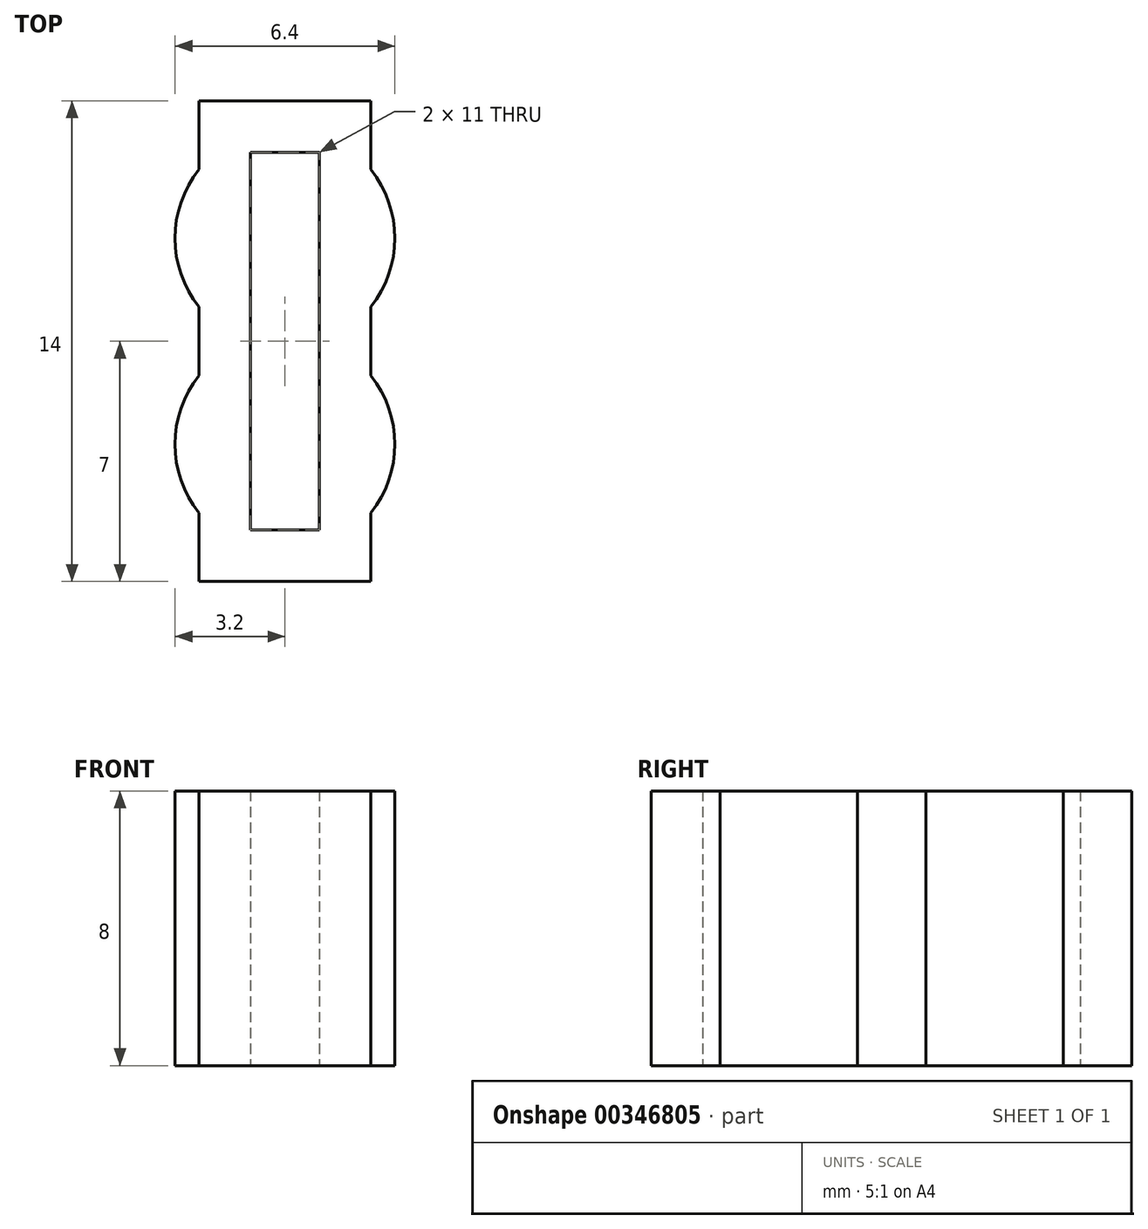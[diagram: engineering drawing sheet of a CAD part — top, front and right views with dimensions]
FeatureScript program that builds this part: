
annotation { "Feature Type Name" : "Feature", "Feature Type Description" : "" }
export const myFeature = defineFeature(function(context is Context, id is Id, definition is map)
    precondition{}
    {
        {
            var Q0;
            Q0=qCreatedBy(makeId("Top.planeOp"),FACE);
            var sketch = newSketch(context, id + "F0", { "sketchPlane" : qUnion([Q0])});
            skLineSegment(sketch, "E0.bottom", {"start": v(-2.5, 7) * mm, "end": v(2.5, 7) * mm});
            skLineSegment(sketch, "E0.top", {"start": v(-2.5, -7) * mm, "end": v(2.5, -7) * mm});
            skLineSegment(sketch, "E0.left", {"start": v(-2.5, 7) * mm, "end": v(-2.5, -7) * mm});
            skLineSegment(sketch, "E0.right", {"start": v(2.5, 7) * mm, "end": v(2.5, -7) * mm});
            skLineSegment(sketch, "E1.bottom", {"start": v(-1, 5.5) * mm, "end": v(1, 5.5) * mm});
            skLineSegment(sketch, "E1.top", {"start": v(-1, -5.5) * mm, "end": v(1, -5.5) * mm});
            skLineSegment(sketch, "E1.left", {"start": v(-1, 5.5) * mm, "end": v(-1, -5.5) * mm});
            skLineSegment(sketch, "E1.right", {"start": v(1, 5.5) * mm, "end": v(1, -5.5) * mm});
            skSolve(sketch);
        }
        {
            var Q0;
            Q0 = qSketchRegion(id + "F0", true);
            extrude(context, id + "F1", {"entities" : qUnion([Q0]), "depth" : 8 * mm});
        }
        {
            var Q0;
            Q0=qCreatedBy(makeId("Top.planeOp"),FACE);
            var sketch = newSketch(context, id + "F2", { "sketchPlane" : qUnion([Q0])});
            skArc(sketch, "E2", {"start": v(2.5, 1) * mm, "mid": v(3.2, 3) * mm, "end": v(2.5, 5) * mm});
            skArc(sketch, "E3", {"start": v(2.5, -5) * mm, "mid": v(3.2, -3) * mm, "end": v(2.5, -1) * mm});
            skLineSegment(sketch, "E4", {"start": v(2.5, 5) * mm, "end": v(2.5, 1) * mm});
            skLineSegment(sketch, "E5", {"start": v(2.5, -1) * mm, "end": v(2.5, -5) * mm});
            skArc(sketch, "E6", {"start": v(-2.5, 5) * mm, "mid": v(-3.2, 3) * mm, "end": v(-2.5, 1) * mm});
            skArc(sketch, "E7", {"start": v(-2.5, -1) * mm, "mid": v(-3.2, -3) * mm, "end": v(-2.5, -5) * mm});
            skLineSegment(sketch, "E8", {"start": v(-2.5, 5) * mm, "end": v(-2.5, 1) * mm});
            skLineSegment(sketch, "E9", {"start": v(-2.5, -1) * mm, "end": v(-2.5, -5) * mm});
            skSolve(sketch);
        }
        {
            var Q0;
            Q0 = qSketchRegion(id + "F2", true);
            extrude(context, id + "F3", {"entities" : qUnion([Q0]), "operationType" : NewBodyOperationType.ADD, "depth" : 8 * mm});
        }
    });
